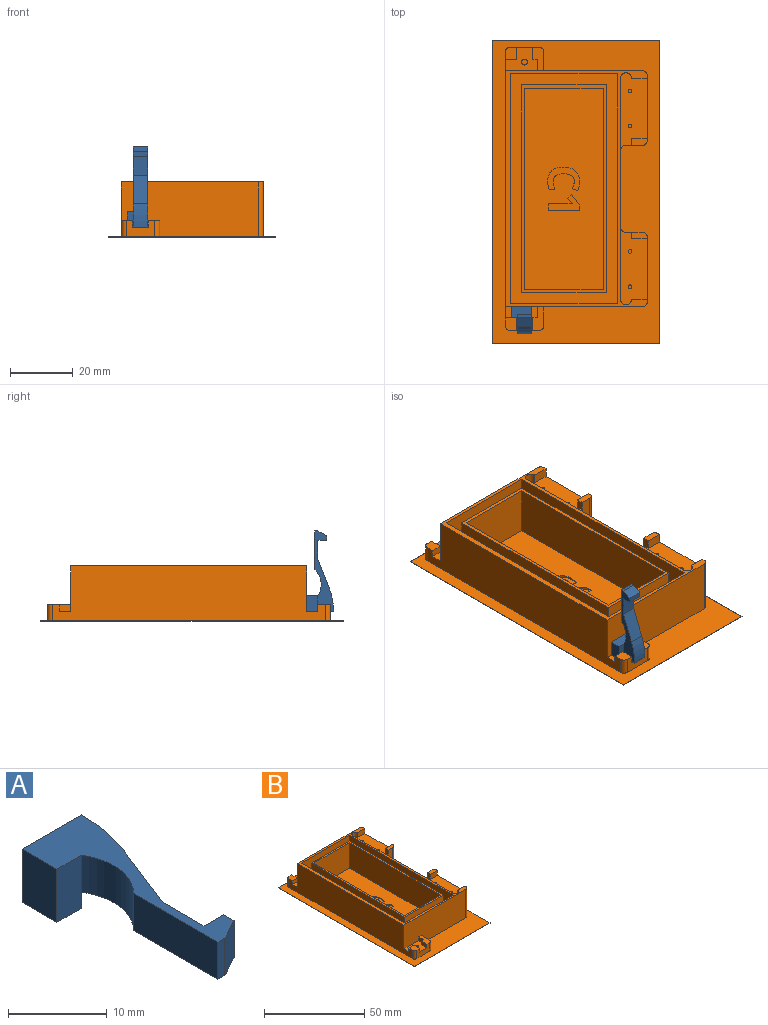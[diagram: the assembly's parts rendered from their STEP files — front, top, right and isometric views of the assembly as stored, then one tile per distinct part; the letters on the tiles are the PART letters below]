
ASSEMBLY  parts=2 mates=1
PART A: 19 faces, bbox 8.5x25.6x6.6 mm
  f0: plane 6.6x3.5mm, normal (0,-1,0), area 23.1mm2, adj f1,f11,f12,f14,f15
  f1: cylinder r=6.83mm len=8.48mm, axis (0,0,-1), area 42.4mm2, adj f0,f2,f12,f13
  f2: plane 12.12x4.6mm, normal (-1,0,0), area 55.7mm2, adj f1,f3,f12,f13
  f3: plane 4.6x1mm, normal (0,-1,0), area 4.6mm2, adj f2,f4,f12,f13
  f4: plane 4.6x2.8mm, normal (0.47,-0.88,0), area 14.6mm2, adj f3,f5,f12,f13
  f5: plane 4.6x1.5mm, normal (1,0,0), area 6.9mm2, adj f4,f6,f12,f13
  f6: plane 4.6x2.8mm, normal (0,1,0), area 12.9mm2, adj f5,f7,f12,f13
  f7: plane 6x4.6mm, normal (1,0,0), area 27.6mm2, adj f6,f8,f12,f13
  f8: plane 9.05x4.6mm, normal (0.93,-0.37,0), area 44.8mm2, adj f7,f12,f13,f18
  f9: plane 4.6x0.18mm, normal (1,0,0), area 0.8mm2, adj f10,f12,f13,f18
  f10: plane 8.5x6.6mm, normal (0,1,0), area 43mm2, adj f9,f11,f12,f13,f14,f15,f16
  f11: plane 6.6x5mm, normal (-1,0,0), area 33mm2, adj f0,f10,f12,f15
  f12: plane 25.6x8.5mm, normal (0,0,1), area 82mm2, adj f0,f1,f2,f3,f4,f5,f6,f7
  f13: plane 25.6x6mm, normal (0,0,-1), area 64.5mm2, adj f1,f2,f3,f4,f5,f6,f7,f8
  f14: plane 5x2mm, normal (1,0,0), area 10mm2, adj f0,f10,f13,f15
  f15: plane 5x3.5mm, normal (0,0,-1), area 17.5mm2, adj f0,f10,f11,f14
  f16: cylinder r=1mm len=4.5mm, axis (0,1,0), area 28.3mm2, adj f10,f17
  f17: plane 2x2mm, normal (0,1,0), area 3.1mm2, adj f16
  f18: cylinder r=20mm len=7.38mm, axis (0,0,-1), area 34.8mm2, adj f8,f9,f12,f13
PART B: 111 faces, bbox 53.2x96x17.5 mm
  f0: plane 64x25mm, normal (0,0,1), area 1540mm2, adj f35,f36,f37,f38,f84,f85,f86,f87
  f1: plane 4x3.55mm, normal (0,0,1), area 13.7mm2, adj f2,f21,f55,f65,f83
  f2: plane 86.83x17.4mm, normal (-1,0,0), area 1349.9mm2, adj f1,f3,f4,f5,f6,f20,f55,f57
  f3: plane 10.34x7.5mm, normal (0,0,1), area 54.4mm2, adj f2,f4,f10,f21,f65,f66,f67,f81
  f4: plane 43.55x17.4mm, normal (0,-1,0), area 717.9mm2, adj f2,f3,f20,f22,f23,f59,f68,f81
  f5: plane 43.55x17.4mm, normal (0,1,0), area 717.9mm2, adj f2,f7,f9,f20,f60,f61,f68,f80
  f6: plane 4x3.55mm, normal (0,0,1), area 13.7mm2, adj f2,f8,f57,f63,f82
  f7: plane 7.5x3.55mm, normal (0,0,1), area 20.5mm2, adj f5,f8,f9,f58,f62,f64,f80
  f8: plane 9.13x5.1mm, normal (0,1,0), area 35.1mm2, adj f6,f7,f57,f58,f61,f62,f63,f68
  f9: plane 5.91x5.1mm, normal (1,0,0), area 30.2mm2, adj f5,f7,f58,f68
  f10: cylinder r=0.9mm len=2.9mm, axis (0,0,1), area 16.4mm2, adj f3,f78
  f11: cylinder r=0.9mm len=2.9mm, axis (0,0,1), area 16.4mm2, adj f61,f77
  f12: plane 17.4x5.33mm, normal (0,1,0), area 86.9mm2, adj f15,f42,f45,f53,f54,f68
  f13: plane 5x3mm, normal (0,1,0), area 15mm2, adj f16,f18,f40,f46
  f14: plane 5x3mm, normal (0,-1,0), area 15mm2, adj f15,f17,f42,f45
  f15: plane 5x2.11mm, normal (0,0,1), area 10mm2, adj f12,f14,f17,f45,f54
  f16: plane 5x2.11mm, normal (0,0,1), area 10mm2, adj f13,f18,f24,f46,f51
  f17: plane 20.52x17.4mm, normal (1,0,0), area 299.5mm2, adj f14,f15,f20,f41,f42,f54,f59,f68
  f18: plane 20.52x17.4mm, normal (1,0,0), area 299.5mm2, adj f13,f16,f20,f39,f40,f51,f60,f68
  f19: plane 66x27mm, normal (0,0,1), area 182mm2, adj f26,f27,f28,f33,f35,f36,f37,f38
  f20: plane 75x45.14mm, normal (0,0,1), area 296mm2, adj f2,f4,f5,f17,f18,f25,f29,f30
  f21: plane 9.13x5.1mm, normal (0,-1,0), area 35.1mm2, adj f1,f3,f23,f55,f56,f65,f66,f68
  f22: plane 5.91x5.1mm, normal (1,0,0), area 30.2mm2, adj f4,f23,f56,f68
  f23: plane 7.5x3.55mm, normal (0,0,1), area 20.5mm2, adj f4,f21,f22,f56,f66,f67,f81
  f24: plane 17.4x5.33mm, normal (0,-1,0), area 86.9mm2, adj f16,f40,f46,f51,f52,f68
  f25: plane 70.23x17.4mm, normal (1,0,0), area 562.5mm2, adj f20,f40,f42,f43,f44,f52,f53,f68
  f26: plane 27x6.4mm, normal (0,-1,0), area 172.8mm2, adj f19,f27,f33,f34
  f27: plane 66x6.4mm, normal (-1,0,0), area 422.4mm2, adj f19,f26,f28,f34
  f28: plane 27x6.4mm, normal (0,1,0), area 172.8mm2, adj f19,f27,f33,f34
  f29: plane 73x6.4mm, normal (1,0,0), area 467.2mm2, adj f20,f30,f32,f34
  f30: plane 34x6.4mm, normal (0,1,0), area 217.6mm2, adj f20,f29,f31,f34
  f31: plane 73x6.4mm, normal (-1,0,0), area 467.2mm2, adj f20,f30,f32,f34
  f32: plane 34x6.4mm, normal (0,-1,0), area 217.6mm2, adj f20,f29,f31,f34
  f33: plane 66x6.4mm, normal (1,0,0), area 422.4mm2, adj f19,f26,f28,f34
  f34: plane 73x34mm, normal (0,0,1), area 700mm2, adj f26,f27,f28,f29,f30,f31,f32,f33
  f35: plane 25x15.5mm, normal (0,-1,0), area 387.5mm2, adj f0,f19,f36,f38
  f36: plane 64x15.5mm, normal (1,0,0), area 992mm2, adj f0,f19,f35,f37
  f37: plane 25x15.5mm, normal (0,1,0), area 387.5mm2, adj f0,f19,f36,f38
  f38: plane 64x15.5mm, normal (-1,0,0), area 992mm2, adj f0,f19,f35,f37
  f39: plane 5x3mm, normal (0,-1,0), area 15mm2, adj f18,f20,f40,f44
  f40: plane 24.65x8.5mm, normal (0,0,1), area 173.9mm2, adj f13,f18,f24,f25,f39,f44,f46,f48
  f41: plane 5x3mm, normal (0,1,0), area 15mm2, adj f17,f20,f42,f43
  f42: plane 24.65x8.5mm, normal (0,0,1), area 173.9mm2, adj f12,f14,f17,f25,f41,f43,f45,f47
  f43: cylinder r=1.75mm len=3.5mm, axis (0,0,1), area 16.5mm2, adj f20,f25,f41,f42
  f44: cylinder r=1.75mm len=3.5mm, axis (0,0,1), area 16.5mm2, adj f20,f25,f39,f40
  f45: plane 3x2.11mm, normal (-1,0,0), area 6.3mm2, adj f12,f14,f15,f42
  f46: plane 3x2.11mm, normal (-1,0,0), area 6.3mm2, adj f13,f16,f24,f40
  f47: cylinder r=0.57mm len=14.4mm, axis (0,0,1), area 51.7mm2, adj f42,f76
  f48: cylinder r=0.57mm len=14.4mm, axis (0,0,1), area 51.7mm2, adj f40,f75
  f49: cylinder r=0.57mm len=14.4mm, axis (0,0,1), area 51.7mm2, adj f40,f74
  f50: cylinder r=0.57mm len=14.4mm, axis (0,0,1), area 51.7mm2, adj f42,f73
  f51: cylinder r=1.59mm len=17.4mm, axis (0,0,-1), area 43.4mm2, adj f16,f18,f24,f68
  f52: cylinder r=1.59mm len=14.4mm, axis (0,0,-1), area 35.9mm2, adj f24,f25,f40,f68
  f53: cylinder r=1.59mm len=14.4mm, axis (0,0,1), area 35.9mm2, adj f12,f25,f42,f68
  f54: cylinder r=1.59mm len=17.4mm, axis (0,0,1), area 43.4mm2, adj f12,f15,f17,f68
  f55: cylinder r=1.59mm len=5.1mm, axis (0,0,1), area 12.7mm2, adj f1,f2,f21,f68
  f56: cylinder r=1.59mm len=5.1mm, axis (0,0,-1), area 12.7mm2, adj f21,f22,f23,f68
  f57: cylinder r=1.59mm len=5.1mm, axis (0,0,1), area 12.7mm2, adj f2,f6,f8,f68
  f58: cylinder r=1.59mm len=5.1mm, axis (0,0,-1), area 12.7mm2, adj f7,f8,f9,f68
  f59: cylinder r=1.59mm len=17.4mm, axis (0,0,1), area 43.4mm2, adj f4,f17,f20,f68
  f60: cylinder r=1.59mm len=17.4mm, axis (0,0,-1), area 43.4mm2, adj f5,f18,f20,f68
  f61: plane 10.34x7.5mm, normal (0,0,1), area 54.4mm2, adj f2,f5,f8,f11,f62,f63,f64,f80
  f62: plane 4x2.2mm, normal (-1,0,0), area 8.8mm2, adj f7,f8,f61,f64
  f63: plane 4x2.2mm, normal (1,0,0), area 8.8mm2, adj f6,f8,f61,f82
  f64: plane 2.2x1.59mm, normal (0,-1,0), area 3.5mm2, adj f7,f61,f62,f80
  f65: plane 4x2.2mm, normal (1,0,0), area 8.8mm2, adj f1,f3,f21,f83
  f66: plane 4x2.2mm, normal (-1,0,0), area 8.8mm2, adj f3,f21,f23,f67
  f67: plane 2.2x1.59mm, normal (0,1,0), area 3.5mm2, adj f3,f23,f66,f81
  f68: plane 96x53.2mm, normal (0,0,1), area 1775mm2, adj f2,f4,f5,f8,f9,f12,f17,f18
  f69: plane 96x0.1mm, normal (1,0,0), area 9.6mm2, adj f68,f70,f72,f79
  f70: plane 53.2x0.1mm, normal (0,-1,0), area 5.3mm2, adj f68,f69,f71,f79
  f71: plane 96x0.1mm, normal (-1,0,0), area 9.6mm2, adj f68,f70,f72,f79
  f72: plane 53.2x0.1mm, normal (0,1,0), area 5.3mm2, adj f68,f69,f71,f79
  f73: plane 1.14x1.14mm, normal (0,0,1), area 1mm2, adj f50
  f74: plane 1.14x1.14mm, normal (0,0,1), area 1mm2, adj f49
  f75: plane 1.14x1.14mm, normal (0,0,1), area 1mm2, adj f48
  f76: plane 1.14x1.14mm, normal (0,0,1), area 1mm2, adj f47
  f77: plane 1.8x1.8mm, normal (0,0,1), area 2.5mm2, adj f11
  f78: plane 1.8x1.8mm, normal (0,0,1), area 2.5mm2, adj f10
  f79: plane 96x53.2mm, normal (0,0,-1), area 5107.2mm2, adj f69,f70,f71,f72
  f80: plane 3.5x2.2mm, normal (-1,0,0), area 7.7mm2, adj f5,f7,f61,f64
  f81: plane 3.5x2.2mm, normal (-1,0,0), area 7.7mm2, adj f3,f4,f23,f67
  f82: plane 3.55x2.2mm, normal (0,-1,0), area 7.8mm2, adj f2,f6,f61,f63
  f83: plane 3.55x2.2mm, normal (0,1,0), area 7.8mm2, adj f1,f2,f3,f65
  f84: plane 2.1x0.5mm, normal (1,0,0), area 1mm2, adj f0,f85,f93,f94
  f85: plane 9.92x0.5mm, normal (0,1,0), area 5mm2, adj f0,f84,f86,f94
  f86: plane 1.72x0.5mm, normal (-1,0,0), area 0.9mm2, adj f0,f85,f87,f94
  f87: plane 3.19x2.54mm, normal (-0.78,-0.62,0), area 2mm2, adj f0,f86,f88,f94
  f88: plane 1.26x1.01mm, normal (0.63,-0.78,0), area 0.8mm2, adj f0,f87,f89,f94
  f89: plane 1.14x0.92mm, normal (0.78,0.63,0), area 0.7mm2, adj f0,f88,f90,f94
  f90: extruded ~0.73x0.68mm, area 0.5mm2, adj f0,f89,f91,f94
  f91: plane 1.03x0.5mm, normal (-0.03,-1,0), area 0.5mm2, adj f0,f90,f92,f94
  f92: plane 0.94x0.5mm, normal (-0.02,-1,0), area 0.5mm2, adj f0,f91,f93,f94
  f93: plane 5.74x0.5mm, normal (0,-1,0), area 2.9mm2, adj f0,f84,f92,f94
  f94: plane 9.92x4.92mm, normal (0,0,1), area 25.4mm2, adj f84,f85,f86,f87,f88,f89,f90,f91
  f95: extruded ~1.84x0.89mm, area 1.1mm2, adj f0,f96,f109,f110
  f96: extruded ~1.1x0.5mm, area 0.6mm2, adj f0,f95,f97,f110
  f97: extruded ~1.12x0.5mm, area 0.6mm2, adj f0,f96,f98,f110
  f98: plane 1.71x0.68mm, normal (0.37,0.93,0), area 0.9mm2, adj f0,f97,f99,f110
  f99: extruded ~2.9x0.7mm, area 1.5mm2, adj f0,f98,f100,f110
  f100: extruded ~2.47x0.62mm, area 1.3mm2, adj f0,f99,f101,f110
  f101: extruded ~1.78x1.62mm, area 1.2mm2, adj f0,f100,f102,f110
  f102: extruded ~2.71x0.56mm, area 1.4mm2, adj f0,f101,f103,f110
  f103: extruded ~3.77x1.15mm, area 2mm2, adj f0,f102,f104,f110
  f104: extruded ~3.31x1.31mm, area 1.8mm2, adj f0,f103,f105,f110
  f105: extruded ~2.73x0.51mm, area 1.4mm2, adj f0,f104,f106,f110
  f106: plane 1.76x0.5mm, normal (0,1,0), area 0.9mm2, adj f0,f105,f107,f110
  f107: extruded ~2.53x0.52mm, area 1.3mm2, adj f0,f106,f108,f110
  f108: extruded ~3.32x2.49mm, area 2.4mm2, adj f0,f107,f109,f110
  f109: extruded ~2.49x0.65mm, area 1.3mm2, adj f0,f95,f108,f110
  f110: plane 10.19x7.55mm, normal (0,0,1), area 34.5mm2, adj f95,f96,f97,f98,f99,f100,f101,f102
PLACE A rot(axis=(-0.58,0.58,-0.58),120deg) t=(-23.13,-39.64,31.09)mm
PLACE B t=(18.16,-37.14,23.09)mm
MATE fastened A.f16 <-> B.f10  axis (0,0,-1) through (-20.83,-39.89,26.09)mm
